# Revit family: Zumtobel PERLUCE O LED
name_source: partatom
category: Lighting Fixtures
revit_build: Autodesk Revit 2016 (Build: 20150220_1215(x64)
units: mm (PartAtom-declared; Revit-internal decimal feet)

## family parameters
Cut with Voids When Loaded = No
Host = Face
Light Source = Yes
OmniClass Number = 23.80.70.11
OmniClass Title = Luminaries for Internal Lighting
Part Type = Normal
Room Calculation Point = No
Round Connector Dimension = Use Diameter
Shared = No

## types (4) — shared parameters
Assembly Code = D5020200
Body = Zumtobel_Metal_White
Color Filter = 16777215
Cover = Zumtobel_PMMA_White_Self_Illumination
Description = Opal diffuser LED luminaires
Dimming Lamp Color Temperature Shift = <None>
Emit Shape Visible in Rendering = No
Emit from Rectangle Length = 120 mm  [stored 0.393701 ft]
Height = 91 mm  [stored 0.298556 ft]
Lamp = LED
Manufacturer = Zumtobel Lighting
Tilt Angle = -90.00°
URL = http://www.zumtobel.com
Voltage = 230 V
Width = 120 mm  [stored 0.393701 ft]
zero-valued in all types: Default Elevation

## per-type parameters (varying)
| type | Apparent Load | Emit from Rectangle Width | Length | Model | Photometric Web File |
| PERLUCE O LED4600-840 L1520 LDE IP50 WH | 45 VA | 1520 mm | 1520 mm | 42182766 | 42182766_(STD_LEO).IES |
| PERLUCE O LED4600-840 L1520 LDE IP54 WH | 45 VA | 1520 mm | 1520 mm | 42182767 | 42182767_(STD_LEO).IES |
| PERLUCE O LED3800-840 L1220 LDE IP54 WH | 36 VA | 1220 mm | 1220 mm | 42182764 | 42182764_(STD_LEO).IES |
| PERLUCE O LED3800-840 L1220 LDE IP50 WH | 36 VA | 1220 mm | 1220 mm | 42182763 | 42182763_(STD_LEO).IES |

note: [stored X ft] marks values corroborated as IEEE doubles in the binary element streams (Revit-internal decimal feet)

## geometry (parser evidence)
native form markers: Sweep x3
no freeform markers — native parametric forms only
